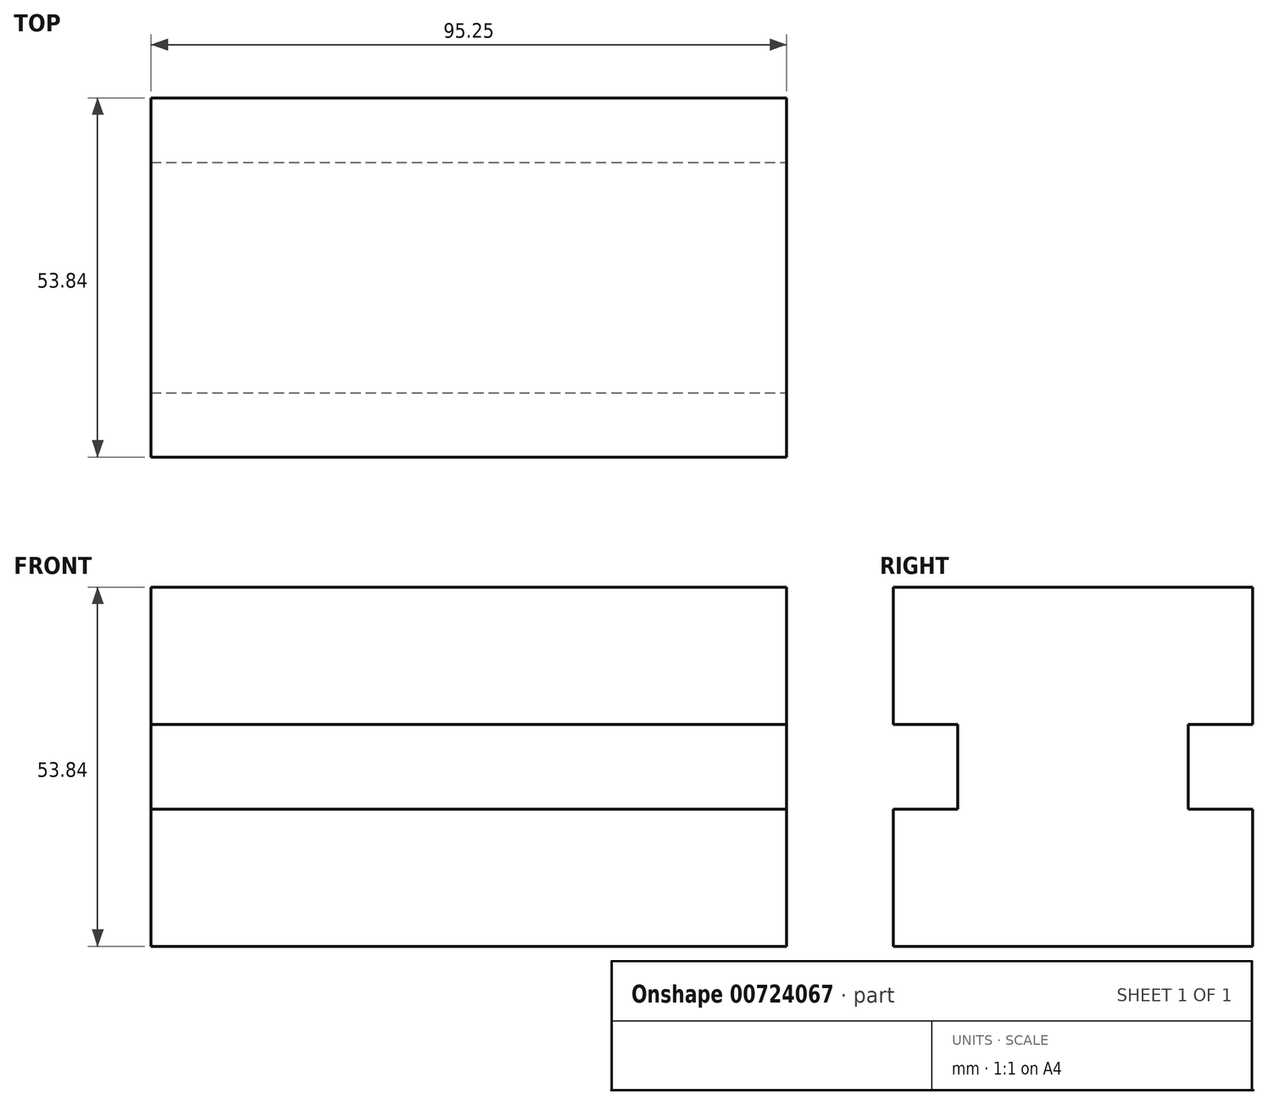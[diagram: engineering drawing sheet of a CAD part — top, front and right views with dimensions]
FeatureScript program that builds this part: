
annotation { "Feature Type Name" : "Feature", "Feature Type Description" : "" }
export const myFeature = defineFeature(function(context is Context, id is Id, definition is map)
    precondition{}
    {
        {
            var Q0;
            Q0=qCreatedBy(makeId("Right.planeOp"),FACE);
            var sketch = newSketch(context, id + "F0", { "sketchPlane" : qUnion([Q0])});
            skLineSegment(sketch, "E0.bottom", {"start": v(26.92, -26.92) * mm, "end": v(-26.92, -26.92) * mm});
            skLineSegment(sketch, "E0.top", {"start": v(26.92, 26.92) * mm, "end": v(-26.92, 26.92) * mm});
            skLineSegment(sketch, "E0.left", {"start": v(26.92, -26.92) * mm, "end": v(26.92, -6.35) * mm});
            skLineSegment(sketch, "E0.right", {"start": v(-26.92, -26.92) * mm, "end": v(-26.92, -6.35) * mm});
            skPoint(sketch, "E0.middle", {"position": v(0, 0) * mm});
            skLineSegment(sketch, "E1.bottom", {"start": v(-26.92, 6.35) * mm, "end": v(-17.27, 6.35) * mm});
            skLineSegment(sketch, "E1.top", {"start": v(-26.92, -6.35) * mm, "end": v(-17.27, -6.35) * mm});
            skLineSegment(sketch, "E1.right", {"start": v(-17.27, 6.35) * mm, "end": v(-17.27, -6.35) * mm});
            skLineSegment(sketch, "E2.trimOffspring", {"start": v(-26.92, 6.35) * mm, "end": v(-26.92, 26.92) * mm});
            skLineSegment(sketch, "E3", {"start": v(0, 36.72) * mm, "end": v(0, -35.38) * mm, "construction": true});
            skLineSegment(sketch, "E4.MirrorCS", {"start": v(26.92, 6.35) * mm, "end": v(17.27, 6.35) * mm});
            skLineSegment(sketch, "E5.MirrorCS", {"start": v(17.27, 6.35) * mm, "end": v(17.27, -6.35) * mm});
            skLineSegment(sketch, "E6.MirrorCS", {"start": v(26.92, -6.35) * mm, "end": v(17.27, -6.35) * mm});
            skLineSegment(sketch, "E7.trimOffspring", {"start": v(26.92, 6.35) * mm, "end": v(26.92, 26.92) * mm});
            skSolve(sketch);
        }
        {
            var Q0;
            Q0=makeQuery(id+"F0.imprint","IMPRINT",FACE,{"disambiguationData":[TD([[makeQuery(id+"F0.imprint","IMPRINT",EDGE,{"derivedFrom":sQuery(id+"F0.wireOp",EDGE,"E0.bottom")}),-1.0]])]});
            extrude(context, id + "F1", {"entities" : qUnion([Q0]), "oppositeDirection" : true, "depth" : 95.25 * mm, "offsetDistance" : 25.4 * mm});
        }
    });
